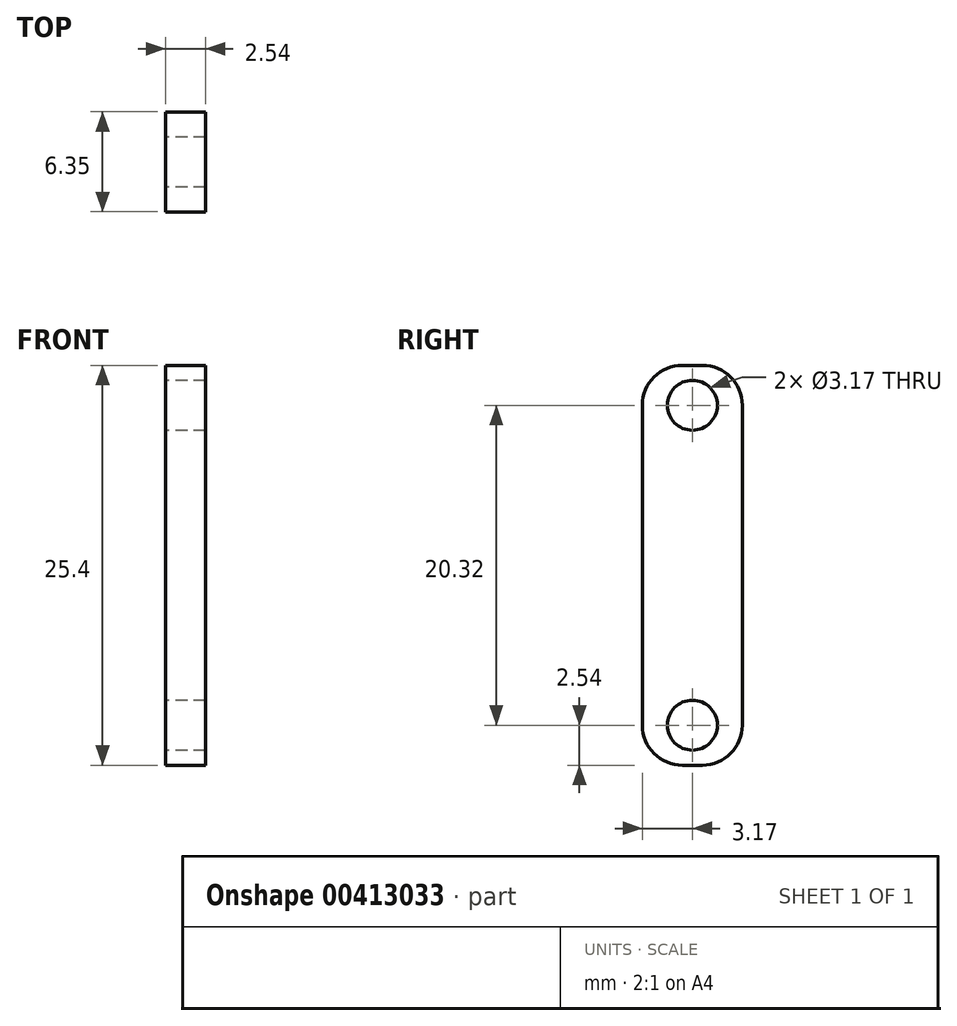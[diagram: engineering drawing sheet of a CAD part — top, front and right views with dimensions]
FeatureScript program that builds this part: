
annotation { "Feature Type Name" : "Feature", "Feature Type Description" : "" }
export const myFeature = defineFeature(function(context is Context, id is Id, definition is map)
    precondition{}
    {
        {
            var Q0;
            Q0=qCreatedBy(makeId("Right.planeOp"),FACE);
            var sketch = newSketch(context, id + "F0", { "sketchPlane" : qUnion([Q0])});
            skLineSegment(sketch, "E0.bottom", {"start": v(0.64, 12.7) * mm, "end": v(-0.63, 12.7) * mm});
            skLineSegment(sketch, "E0.top", {"start": v(0.64, -12.7) * mm, "end": v(-0.63, -12.7) * mm});
            skLineSegment(sketch, "E0.left", {"start": v(3.18, 10.16) * mm, "end": v(3.18, -10.16) * mm});
            skLineSegment(sketch, "E0.right", {"start": v(-3.17, 10.16) * mm, "end": v(-3.17, -10.16) * mm});
            skPoint(sketch, "E0.middle", {"position": v(0, 0) * mm});
            skPoint(sketch, "E1.visualSharp", {"position": v(3.18, -12.7) * mm});
            skArc(sketch, "E1.filletArc", {"start": v(0.64, -12.7) * mm, "mid": v(2.43, -11.96) * mm, "end": v(3.18, -10.16) * mm});
            skPoint(sketch, "E2.visualSharp", {"position": v(-3.17, -12.7) * mm});
            skArc(sketch, "E2.filletArc", {"start": v(-3.17, -10.16) * mm, "mid": v(-2.43, -11.96) * mm, "end": v(-0.63, -12.7) * mm});
            skPoint(sketch, "E3.visualSharp", {"position": v(-3.17, 12.7) * mm});
            skArc(sketch, "E3.filletArc", {"start": v(-0.63, 12.7) * mm, "mid": v(-2.43, 11.96) * mm, "end": v(-3.17, 10.16) * mm});
            skPoint(sketch, "E4.visualSharp", {"position": v(3.18, 12.7) * mm});
            skArc(sketch, "E4.filletArc", {"start": v(3.18, 10.16) * mm, "mid": v(2.43, 11.96) * mm, "end": v(0.64, 12.7) * mm});
            skCircle(sketch, "E5", {"center": v(0, 10.16) * mm, "radius": 1.59 * mm});
            skCircle(sketch, "E6", {"center": v(0, -10.16) * mm, "radius": 1.59 * mm});
            skSolve(sketch);
        }
        {
            var Q0;
            Q0 = qSketchRegion(id + "F0", true);
            extrude(context, id + "F1", {"entities" : qUnion([Q0]), "depth" : 2.54 * mm});
        }
    });
